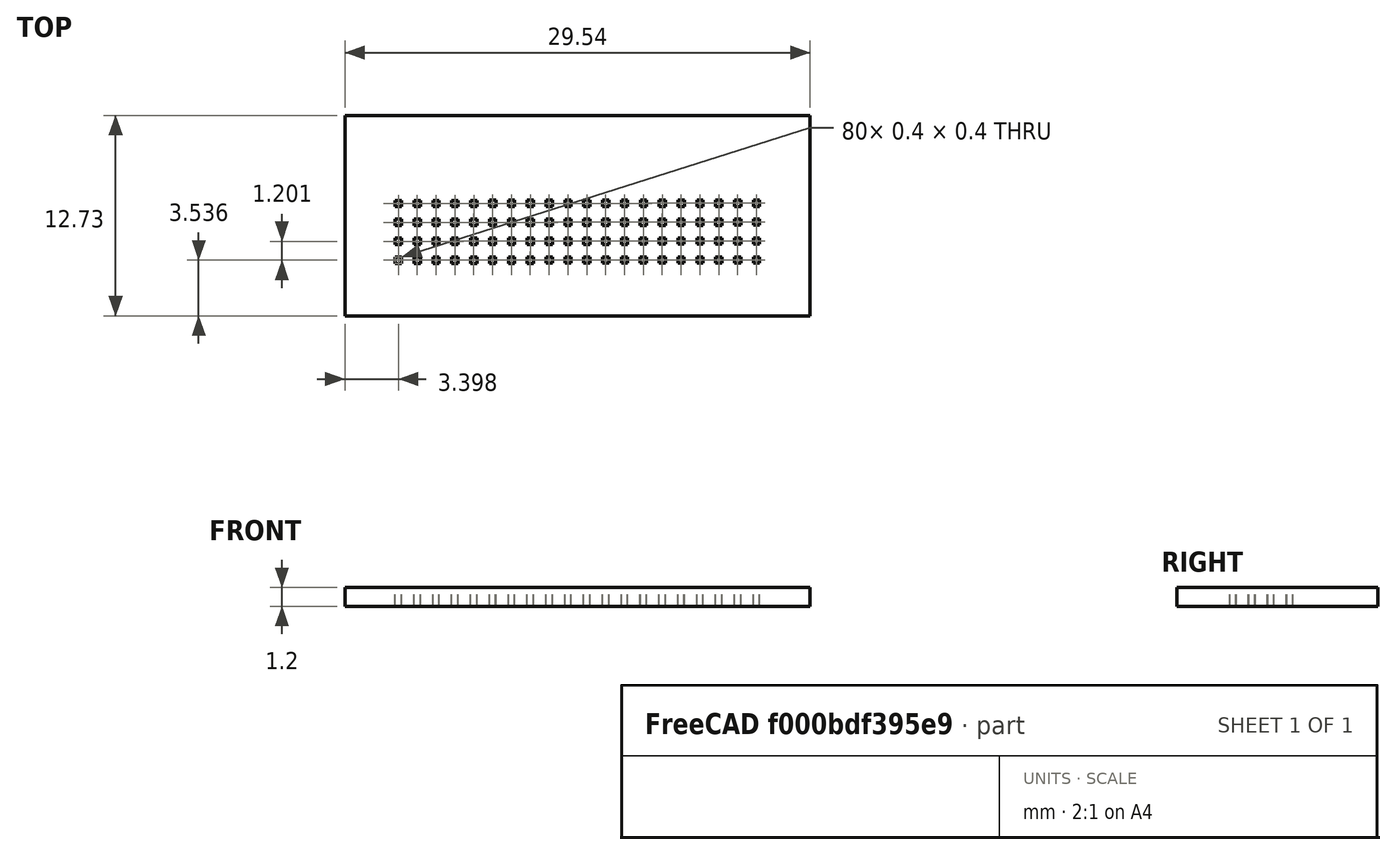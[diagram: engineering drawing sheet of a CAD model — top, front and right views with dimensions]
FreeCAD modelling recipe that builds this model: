
FCSTD DOCUMENT  (FreeCAD 0.17R13519 (Git))
Label: base
License: All rights reserved
LicenseURL: http://en.wikipedia.org/wiki/All_rights_reserved
objects: Sketcher::SketchObject×1, PartDesign::Pad×1, PartDesign::Body×1
note: 4 computed .brp shape members not serialized (recipe doc carries the construction recipe); baked Part::Feature solids carry a one-line shape summary decoded from their .brp

FEATURE [Sketcher::SketchObject] Sketch
  MapMode = 5
  Support = -> [XY_Plane]
  sketch-geometry (335):
    g0: LineSegment [constr] StartX=0 StartY=0 StartZ=0 EndX=31.2 EndY=0 EndZ=0
    g1: LineSegment [constr] StartX=31.2 StartY=0 StartZ=0 EndX=31.2 EndY=31.2 EndZ=0
    g2: LineSegment [constr] StartX=31.2 StartY=31.2 StartZ=0 EndX=0 EndY=31.2 EndZ=0
    g3: LineSegment [constr] StartX=0 StartY=31.2 StartZ=0 EndX=0 EndY=0 EndZ=0
    g4: LineSegment [constr] StartX=4 StartY=4 StartZ=0 EndX=27.2 EndY=4 EndZ=0
    g5: LineSegment [constr] StartX=27.2 StartY=4 StartZ=0 EndX=27.2 EndY=27.2 EndZ=0
    g6: LineSegment [constr] StartX=27.2 StartY=27.2 StartZ=0 EndX=4 EndY=27.2 EndZ=0
    g7: LineSegment [constr] StartX=4 StartY=27.2 StartZ=0 EndX=4 EndY=4 EndZ=0
    g8: LineSegment [constr] StartX=26.74 StartY=26.0196 StartZ=0 EndX=26.74 EndY=25.6196 EndZ=0
    g9: LineSegment [constr] StartX=5.2 StartY=27.2 StartZ=0 EndX=5.2 EndY=28.4271 EndZ=0
    g10: LineSegment StartX=4 StartY=27.2 StartZ=0 EndX=4.4 EndY=27.2 EndZ=0
    g11: LineSegment StartX=4.4 StartY=27.2 StartZ=0 EndX=4.4 EndY=26.8 EndZ=0
    g12: LineSegment StartX=4.4 StartY=26.8 StartZ=0 EndX=4 EndY=26.8 EndZ=0
    g13: LineSegment StartX=4 StartY=26.8 StartZ=0 EndX=4 EndY=27.2 EndZ=0
    g14: LineSegment [constr] StartX=5.2 StartY=26.8 StartZ=0 EndX=5.2 EndY=25.7987 EndZ=0
    g15: LineSegment StartX=5.19695 StartY=27.201 StartZ=0 EndX=5.59695 EndY=27.201 EndZ=0
    g16: LineSegment StartX=5.59695 StartY=27.201 StartZ=0 EndX=5.59695 EndY=26.801 EndZ=0
    g17: LineSegment StartX=5.59695 StartY=26.801 StartZ=0 EndX=5.19695 EndY=26.801 EndZ=0
    g18: LineSegment StartX=5.19695 StartY=26.801 StartZ=0 EndX=5.19695 EndY=27.201 EndZ=0
    g19: LineSegment StartX=6.39391 StartY=27.2021 StartZ=0 EndX=6.79391 EndY=27.2021 EndZ=0
    g20: LineSegment StartX=6.79391 StartY=27.2021 StartZ=0 EndX=6.79391 EndY=26.8021 EndZ=0
    g21: LineSegment StartX=6.79391 StartY=26.8021 StartZ=0 EndX=6.39391 EndY=26.8021 EndZ=0
    g22: LineSegment StartX=6.39391 StartY=26.8021 StartZ=0 EndX=6.39391 EndY=27.2021 EndZ=0
    g23: LineSegment StartX=7.59086 StartY=27.2031 StartZ=0 EndX=7.99086 EndY=27.2031 EndZ=0
    g24: LineSegment StartX=7.99086 StartY=27.2031 StartZ=0 EndX=7.99086 EndY=26.8031 EndZ=0
    g25: LineSegment StartX=7.99086 StartY=26.8031 StartZ=0 EndX=7.59086 EndY=26.8031 EndZ=0
    g26: LineSegment StartX=7.59086 StartY=26.8031 StartZ=0 EndX=7.59086 EndY=27.2031 EndZ=0
    g27: LineSegment StartX=8.78782 StartY=27.2041 StartZ=0 EndX=9.18782 EndY=27.2041 EndZ=0
    g28: LineSegment StartX=9.18782 StartY=27.2041 StartZ=0 EndX=9.18782 EndY=26.8041 EndZ=0
    g29: LineSegment StartX=9.18782 StartY=26.8041 StartZ=0 EndX=8.78782 EndY=26.8041 EndZ=0
    g30: LineSegment StartX=8.78782 StartY=26.8041 StartZ=0 EndX=8.78782 EndY=27.2041 EndZ=0
    g31: LineSegment StartX=9.98477 StartY=27.2052 StartZ=0 EndX=10.3848 EndY=27.2052 EndZ=0
    g32: LineSegment StartX=10.3848 StartY=27.2052 StartZ=0 EndX=10.3848 EndY=26.8052 EndZ=0
    g33: LineSegment StartX=10.3848 StartY=26.8052 StartZ=0 EndX=9.98477 EndY=26.8052 EndZ=0
    g34: LineSegment StartX=9.98477 StartY=26.8052 StartZ=0 EndX=9.98477 EndY=27.2052 EndZ=0
    g35: LineSegment StartX=11.1817 StartY=27.2062 StartZ=0 EndX=11.5817 EndY=27.2062 EndZ=0
    g36: LineSegment StartX=11.5817 StartY=27.2062 StartZ=0 EndX=11.5817 EndY=26.8062 EndZ=0
    g37: LineSegment StartX=11.5817 StartY=26.8062 StartZ=0 EndX=11.1817 EndY=26.8062 EndZ=0
    g38: LineSegment StartX=11.1817 StartY=26.8062 StartZ=0 EndX=11.1817 EndY=27.2062 EndZ=0
    g39: LineSegment StartX=12.3787 StartY=27.2072 StartZ=0 EndX=12.7787 EndY=27.2072 EndZ=0
    g40: LineSegment StartX=12.7787 StartY=27.2072 StartZ=0 EndX=12.7787 EndY=26.8072 EndZ=0
    g41: LineSegment StartX=12.7787 StartY=26.8072 StartZ=0 EndX=12.3787 EndY=26.8072 EndZ=0
    g42: LineSegment StartX=12.3787 StartY=26.8072 StartZ=0 EndX=12.3787 EndY=27.2072 EndZ=0
    g43: LineSegment StartX=13.5756 StartY=27.2083 StartZ=0 EndX=13.9756 EndY=27.2083 EndZ=0
    g44: LineSegment StartX=13.9756 StartY=27.2083 StartZ=0 EndX=13.9756 EndY=26.8083 EndZ=0
    g45: LineSegment StartX=13.9756 StartY=26.8083 StartZ=0 EndX=13.5756 EndY=26.8083 EndZ=0
    g46: LineSegment StartX=13.5756 StartY=26.8083 StartZ=0 EndX=13.5756 EndY=27.2083 EndZ=0
    g47: LineSegment StartX=14.7726 StartY=27.2093 StartZ=0 EndX=15.1726 EndY=27.2093 EndZ=0
    g48: LineSegment StartX=15.1726 StartY=27.2093 StartZ=0 EndX=15.1726 EndY=26.8093 EndZ=0
    g49: LineSegment StartX=15.1726 StartY=26.8093 StartZ=0 EndX=14.7726 EndY=26.8093 EndZ=0
    g50: LineSegment StartX=14.7726 StartY=26.8093 StartZ=0 EndX=14.7726 EndY=27.2093 EndZ=0
    g51: LineSegment StartX=15.9695 StartY=27.2103 StartZ=0 EndX=16.3695 EndY=27.2103 EndZ=0
    g52: LineSegment StartX=16.3695 StartY=27.2103 StartZ=0 EndX=16.3695 EndY=26.8103 EndZ=0
    g53: LineSegment StartX=16.3695 StartY=26.8103 StartZ=0 EndX=15.9695 EndY=26.8103 EndZ=0
    g54: LineSegment StartX=15.9695 StartY=26.8103 StartZ=0 EndX=15.9695 EndY=27.2103 EndZ=0
    g55: LineSegment StartX=17.1665 StartY=27.2114 StartZ=0 EndX=17.5665 EndY=27.2114 EndZ=0
    g56: LineSegment StartX=17.5665 StartY=27.2114 StartZ=0 EndX=17.5665 EndY=26.8114 EndZ=0
    g57: LineSegment StartX=17.5665 StartY=26.8114 StartZ=0 EndX=17.1665 EndY=26.8114 EndZ=0
    g58: LineSegment StartX=17.1665 StartY=26.8114 StartZ=0 EndX=17.1665 EndY=27.2114 EndZ=0
    g59: LineSegment StartX=18.3634 StartY=27.2124 StartZ=0 EndX=18.7634 EndY=27.2124 EndZ=0
    g60: LineSegment StartX=18.7634 StartY=27.2124 StartZ=0 EndX=18.7634 EndY=26.8124 EndZ=0
    g61: LineSegment StartX=18.7634 StartY=26.8124 StartZ=0 EndX=18.3634 EndY=26.8124 EndZ=0
    g62: LineSegment StartX=18.3634 StartY=26.8124 StartZ=0 EndX=18.3634 EndY=27.2124 EndZ=0
    g63: LineSegment StartX=19.5604 StartY=27.2134 StartZ=0 EndX=19.9604 EndY=27.2134 EndZ=0
    g64: LineSegment StartX=19.9604 StartY=27.2134 StartZ=0 EndX=19.9604 EndY=26.8134 EndZ=0
    g65: LineSegment StartX=19.9604 StartY=26.8134 StartZ=0 EndX=19.5604 EndY=26.8134 EndZ=0
    g66: LineSegment StartX=19.5604 StartY=26.8134 StartZ=0 EndX=19.5604 EndY=27.2134 EndZ=0
    g67: LineSegment StartX=20.7574 StartY=27.2144 StartZ=0 EndX=21.1574 EndY=27.2144 EndZ=0
    g68: LineSegment StartX=21.1574 StartY=27.2144 StartZ=0 EndX=21.1574 EndY=26.8144 EndZ=0
    g69: LineSegment StartX=21.1574 StartY=26.8144 StartZ=0 EndX=20.7574 EndY=26.8144 EndZ=0
    g70: LineSegment StartX=20.7574 StartY=26.8144 StartZ=0 EndX=20.7574 EndY=27.2144 EndZ=0
    g71: LineSegment StartX=21.9543 StartY=27.2155 StartZ=0 EndX=22.3543 EndY=27.2155 EndZ=0
    g72: LineSegment StartX=22.3543 StartY=27.2155 StartZ=0 EndX=22.3543 EndY=26.8155 EndZ=0
    g73: LineSegment StartX=22.3543 StartY=26.8155 StartZ=0 EndX=21.9543 EndY=26.8155 EndZ=0
    g74: LineSegment StartX=21.9543 StartY=26.8155 StartZ=0 EndX=21.9543 EndY=27.2155 EndZ=0
    g75: LineSegment StartX=23.1513 StartY=27.2165 StartZ=0 EndX=23.5513 EndY=27.2165 EndZ=0
    g76: LineSegment StartX=23.5513 StartY=27.2165 StartZ=0 EndX=23.5513 EndY=26.8165 EndZ=0
    g77: LineSegment StartX=23.5513 StartY=26.8165 StartZ=0 EndX=23.1513 EndY=26.8165 EndZ=0
    g78: LineSegment StartX=23.1513 StartY=26.8165 StartZ=0 EndX=23.1513 EndY=27.2165 EndZ=0
    g79: LineSegment StartX=24.3482 StartY=27.2175 StartZ=0 EndX=24.7482 EndY=27.2175 EndZ=0
    g80: LineSegment StartX=24.7482 StartY=27.2175 StartZ=0 EndX=24.7482 EndY=26.8175 EndZ=0
    g81: LineSegment StartX=24.7482 StartY=26.8175 StartZ=0 EndX=24.3482 EndY=26.8175 EndZ=0
    g82: LineSegment StartX=24.3482 StartY=26.8175 StartZ=0 EndX=24.3482 EndY=27.2175 EndZ=0
    g83: LineSegment StartX=25.5452 StartY=27.2186 StartZ=0 EndX=25.9452 EndY=27.2186 EndZ=0
    g84: LineSegment StartX=25.9452 StartY=27.2186 StartZ=0 EndX=25.9452 EndY=26.8186 EndZ=0
    g85: LineSegment StartX=25.9452 StartY=26.8186 StartZ=0 EndX=25.5452 EndY=26.8186 EndZ=0
    g86: LineSegment StartX=25.5452 StartY=26.8186 StartZ=0 EndX=25.5452 EndY=27.2186 EndZ=0
    g87: LineSegment StartX=26.74 StartY=27.2196 StartZ=0 EndX=27.1421 EndY=27.2196 EndZ=0
    g88: LineSegment StartX=27.1421 StartY=27.2196 StartZ=0 EndX=27.1421 EndY=26.8196 EndZ=0
    g89: LineSegment StartX=27.1421 StartY=26.8196 StartZ=0 EndX=26.74 EndY=26.8196 EndZ=0
    g90: LineSegment StartX=26.74 StartY=26.8196 StartZ=0 EndX=26.74 EndY=27.2196 EndZ=0
    g91: LineSegment StartX=3.99932 StartY=25.9988 StartZ=0 EndX=4.39932 EndY=25.9988 EndZ=0
    g92: LineSegment StartX=4.39932 StartY=25.9988 StartZ=0 EndX=4.39932 EndY=25.5988 EndZ=0
    g93: LineSegment StartX=4.39932 StartY=25.5988 StartZ=0 EndX=3.99932 EndY=25.5988 EndZ=0
    g94: LineSegment StartX=3.99932 StartY=25.5988 StartZ=0 EndX=3.99932 EndY=25.9988 EndZ=0
    g95: LineSegment StartX=5.19627 StartY=25.9998 StartZ=0 EndX=5.59627 EndY=25.9998 EndZ=0
    g96: LineSegment StartX=5.59627 StartY=25.9998 StartZ=0 EndX=5.59627 EndY=25.5998 EndZ=0
    g97: LineSegment StartX=5.59627 StartY=25.5998 StartZ=0 EndX=5.19627 EndY=25.5998 EndZ=0
    g98: LineSegment StartX=5.19627 StartY=25.5998 StartZ=0 EndX=5.19627 EndY=25.9998 EndZ=0
    g99: LineSegment StartX=6.39322 StartY=26.0009 StartZ=0 EndX=6.79322 EndY=26.0009 EndZ=0
    g100: LineSegment StartX=6.79322 StartY=26.0009 StartZ=0 EndX=6.79322 EndY=25.6009 EndZ=0
    g101: LineSegment StartX=6.79322 StartY=25.6009 StartZ=0 EndX=6.39322 EndY=25.6009 EndZ=0
    g102: LineSegment StartX=6.39322 StartY=25.6009 StartZ=0 EndX=6.39322 EndY=26.0009 EndZ=0
    g103: LineSegment StartX=7.59018 StartY=26.0019 StartZ=0 EndX=7.99018 EndY=26.0019 EndZ=0
    g104: LineSegment StartX=7.99018 StartY=26.0019 StartZ=0 EndX=7.99018 EndY=25.6019 EndZ=0
    g105: LineSegment StartX=7.99018 StartY=25.6019 StartZ=0 EndX=7.59018 EndY=25.6019 EndZ=0
    g106: LineSegment StartX=7.59018 StartY=25.6019 StartZ=0 EndX=7.59018 EndY=26.0019 EndZ=0
    g107: LineSegment StartX=8.78713 StartY=26.0029 StartZ=0 EndX=9.18713 EndY=26.0029 EndZ=0
    g108: LineSegment StartX=9.18713 StartY=26.0029 StartZ=0 EndX=9.18713 EndY=25.6029 EndZ=0
    g109: LineSegment StartX=9.18713 StartY=25.6029 StartZ=0 EndX=8.78713 EndY=25.6029 EndZ=0
    g110: LineSegment StartX=8.78713 StartY=25.6029 StartZ=0 EndX=8.78713 EndY=26.0029 EndZ=0
    g111: LineSegment StartX=9.98409 StartY=26.004 StartZ=0 EndX=10.3841 EndY=26.004 EndZ=0
    g112: LineSegment StartX=10.3841 StartY=26.004 StartZ=0 EndX=10.3841 EndY=25.604 EndZ=0
    g113: LineSegment StartX=10.3841 StartY=25.604 StartZ=0 EndX=9.98409 EndY=25.604 EndZ=0
    g114: LineSegment StartX=9.98409 StartY=25.604 StartZ=0 EndX=9.98409 EndY=26.004 EndZ=0
    g115: LineSegment StartX=11.181 StartY=26.005 StartZ=0 EndX=11.581 EndY=26.005 EndZ=0
    g116: LineSegment StartX=11.581 StartY=26.005 StartZ=0 EndX=11.581 EndY=25.605 EndZ=0
    g117: LineSegment StartX=11.581 StartY=25.605 StartZ=0 EndX=11.181 EndY=25.605 EndZ=0
    g118: LineSegment StartX=11.181 StartY=25.605 StartZ=0 EndX=11.181 EndY=26.005 EndZ=0
    g119: LineSegment StartX=12.378 StartY=26.006 StartZ=0 EndX=12.778 EndY=26.006 EndZ=0
    g120: LineSegment StartX=12.778 StartY=26.006 StartZ=0 EndX=12.778 EndY=25.606 EndZ=0
    g121: LineSegment StartX=12.778 StartY=25.606 StartZ=0 EndX=12.378 EndY=25.606 EndZ=0
    g122: LineSegment StartX=12.378 StartY=25.606 StartZ=0 EndX=12.378 EndY=26.006 EndZ=0
    g123: LineSegment StartX=13.5749 StartY=26.0071 StartZ=0 EndX=13.9749 EndY=26.0071 EndZ=0
    g124: LineSegment StartX=13.9749 StartY=26.0071 StartZ=0 EndX=13.9749 EndY=25.6071 EndZ=0
    g125: LineSegment StartX=13.9749 StartY=25.6071 StartZ=0 EndX=13.5749 EndY=25.6071 EndZ=0
    g126: LineSegment StartX=13.5749 StartY=25.6071 StartZ=0 EndX=13.5749 EndY=26.0071 EndZ=0
    g127: LineSegment StartX=14.7719 StartY=26.0081 StartZ=0 EndX=15.1719 EndY=26.0081 EndZ=0
    g128: LineSegment StartX=15.1719 StartY=26.0081 StartZ=0 EndX=15.1719 EndY=25.6081 EndZ=0
    g129: LineSegment StartX=15.1719 StartY=25.6081 StartZ=0 EndX=14.7719 EndY=25.6081 EndZ=0
    g130: LineSegment StartX=14.7719 StartY=25.6081 StartZ=0 EndX=14.7719 EndY=26.0081 EndZ=0
    g131: LineSegment StartX=15.9689 StartY=26.0091 StartZ=0 EndX=16.3689 EndY=26.0091 EndZ=0
    g132: LineSegment StartX=16.3689 StartY=26.0091 StartZ=0 EndX=16.3689 EndY=25.6091 EndZ=0
    g133: LineSegment StartX=16.3689 StartY=25.6091 StartZ=0 EndX=15.9689 EndY=25.6091 EndZ=0
    g134: LineSegment StartX=15.9689 StartY=25.6091 StartZ=0 EndX=15.9689 EndY=26.0091 EndZ=0
    g135: LineSegment StartX=17.1658 StartY=26.0102 StartZ=0 EndX=17.5658 EndY=26.0102 EndZ=0
    g136: LineSegment StartX=17.5658 StartY=26.0102 StartZ=0 EndX=17.5658 EndY=25.6102 EndZ=0
    g137: LineSegment StartX=17.5658 StartY=25.6102 StartZ=0 EndX=17.1658 EndY=25.6102 EndZ=0
    g138: LineSegment StartX=17.1658 StartY=25.6102 StartZ=0 EndX=17.1658 EndY=26.0102 EndZ=0
    g139: LineSegment StartX=18.3628 StartY=26.0112 StartZ=0 EndX=18.7628 EndY=26.0112 EndZ=0
    g140: LineSegment StartX=18.7628 StartY=26.0112 StartZ=0 EndX=18.7628 EndY=25.6112 EndZ=0
    g141: LineSegment StartX=18.7628 StartY=25.6112 StartZ=0 EndX=18.3628 EndY=25.6112 EndZ=0
    g142: LineSegment StartX=18.3628 StartY=25.6112 StartZ=0 EndX=18.3628 EndY=26.0112 EndZ=0
    g143: LineSegment StartX=19.5597 StartY=26.0122 StartZ=0 EndX=19.9597 EndY=26.0122 EndZ=0
    g144: LineSegment StartX=19.9597 StartY=26.0122 StartZ=0 EndX=19.9597 EndY=25.6122 EndZ=0
    g145: LineSegment StartX=19.9597 StartY=25.6122 StartZ=0 EndX=19.5597 EndY=25.6122 EndZ=0
    g146: LineSegment StartX=19.5597 StartY=25.6122 StartZ=0 EndX=19.5597 EndY=26.0122 EndZ=0
    g147: LineSegment StartX=20.7567 StartY=26.0132 StartZ=0 EndX=21.1567 EndY=26.0132 EndZ=0
    g148: LineSegment StartX=21.1567 StartY=26.0132 StartZ=0 EndX=21.1567 EndY=25.6132 EndZ=0
    g149: LineSegment StartX=21.1567 StartY=25.6132 StartZ=0 EndX=20.7567 EndY=25.6132 EndZ=0
    g150: LineSegment StartX=20.7567 StartY=25.6132 StartZ=0 EndX=20.7567 EndY=26.0132 EndZ=0
    g151: LineSegment StartX=21.9536 StartY=26.0143 StartZ=0 EndX=22.3536 EndY=26.0143 EndZ=0
    g152: LineSegment StartX=22.3536 StartY=26.0143 StartZ=0 EndX=22.3536 EndY=25.6143 EndZ=0
    g153: LineSegment StartX=22.3536 StartY=25.6143 StartZ=0 EndX=21.9536 EndY=25.6143 EndZ=0
    g154: LineSegment StartX=21.9536 StartY=25.6143 StartZ=0 EndX=21.9536 EndY=26.0143 EndZ=0
    g155: LineSegment StartX=23.1506 StartY=26.0153 StartZ=0 EndX=23.5506 EndY=26.0153 EndZ=0
    g156: LineSegment StartX=23.5506 StartY=26.0153 StartZ=0 EndX=23.5506 EndY=25.6153 EndZ=0
    g157: LineSegment StartX=23.5506 StartY=25.6153 StartZ=0 EndX=23.1506 EndY=25.6153 EndZ=0
    g158: LineSegment StartX=23.1506 StartY=25.6153 StartZ=0 EndX=23.1506 EndY=26.0153 EndZ=0
    g159: LineSegment StartX=24.3475 StartY=26.0163 StartZ=0 EndX=24.7475 EndY=26.0163 EndZ=0
    g160: LineSegment StartX=24.7475 StartY=26.0163 StartZ=0 EndX=24.7475 EndY=25.6163 EndZ=0
    g161: LineSegment StartX=24.7475 StartY=25.6163 StartZ=0 EndX=24.3475 EndY=25.6163 EndZ=0
    g162: LineSegment StartX=24.3475 StartY=25.6163 StartZ=0 EndX=24.3475 EndY=26.0163 EndZ=0
    g163: LineSegment StartX=25.5445 StartY=26.0174 StartZ=0 EndX=25.9445 EndY=26.0174 EndZ=0
    g164: LineSegment StartX=25.9445 StartY=26.0174 StartZ=0 EndX=25.9445 EndY=25.6174 EndZ=0
    g165: LineSegment StartX=25.9445 StartY=25.6174 StartZ=0 EndX=25.5445 EndY=25.6174 EndZ=0
    g166: LineSegment StartX=25.5445 StartY=25.6174 StartZ=0 EndX=25.5445 EndY=26.0174 EndZ=0
    g167: LineSegment StartX=26.74 StartY=26.0184 StartZ=0 EndX=27.1414 EndY=26.0184 EndZ=0
    g168: LineSegment StartX=27.1414 StartY=26.0184 StartZ=0 EndX=27.1414 EndY=25.6196 EndZ=0
    g169: LineSegment StartX=27.1414 StartY=25.6196 StartZ=0 EndX=26.74 EndY=25.6196 EndZ=0
    g170: LineSegment StartX=26.74 StartY=25.6196 StartZ=0 EndX=26.74 EndY=26.0184 EndZ=0
    g171: LineSegment StartX=3.99863 StartY=24.7976 StartZ=0 EndX=4.39863 EndY=24.7976 EndZ=0
    g172: LineSegment StartX=4.39863 StartY=24.7976 StartZ=0 EndX=4.39863 EndY=24.3976 EndZ=0
    g173: LineSegment StartX=4.39863 StartY=24.3976 StartZ=0 EndX=3.99863 EndY=24.3976 EndZ=0
    g174: LineSegment StartX=3.99863 StartY=24.3976 StartZ=0 EndX=3.99863 EndY=24.7976 EndZ=0
    g175: LineSegment StartX=5.19559 StartY=24.7986 StartZ=0 EndX=5.59559 EndY=24.7986 EndZ=0
    g176: LineSegment StartX=5.59559 StartY=24.7986 StartZ=0 EndX=5.59559 EndY=24.3986 EndZ=0
    g177: LineSegment StartX=5.59559 StartY=24.3986 StartZ=0 EndX=5.19559 EndY=24.3986 EndZ=0
    g178: LineSegment StartX=5.19559 StartY=24.3986 StartZ=0 EndX=5.19559 EndY=24.7986 EndZ=0
    g179: LineSegment StartX=6.39254 StartY=24.7997 StartZ=0 EndX=6.79254 EndY=24.7997 EndZ=0
    g180: LineSegment StartX=6.79254 StartY=24.7997 StartZ=0 EndX=6.79254 EndY=24.3997 EndZ=0
    g181: LineSegment StartX=6.79254 StartY=24.3997 StartZ=0 EndX=6.39254 EndY=24.3997 EndZ=0
    g182: LineSegment StartX=6.39254 StartY=24.3997 StartZ=0 EndX=6.39254 EndY=24.7997 EndZ=0
    g183: LineSegment StartX=7.58949 StartY=24.8007 StartZ=0 EndX=7.98949 EndY=24.8007 EndZ=0
    g184: LineSegment StartX=7.98949 StartY=24.8007 StartZ=0 EndX=7.98949 EndY=24.4007 EndZ=0
    g185: LineSegment StartX=7.98949 StartY=24.4007 StartZ=0 EndX=7.58949 EndY=24.4007 EndZ=0
    g186: LineSegment StartX=7.58949 StartY=24.4007 StartZ=0 EndX=7.58949 EndY=24.8007 EndZ=0
    g187: LineSegment StartX=8.78645 StartY=24.8017 StartZ=0 EndX=9.18645 EndY=24.8017 EndZ=0
    g188: LineSegment StartX=9.18645 StartY=24.8017 StartZ=0 EndX=9.18645 EndY=24.4017 EndZ=0
    g189: LineSegment StartX=9.18645 StartY=24.4017 StartZ=0 EndX=8.78645 EndY=24.4017 EndZ=0
    g190: LineSegment StartX=8.78645 StartY=24.4017 StartZ=0 EndX=8.78645 EndY=24.8017 EndZ=0
    g191: LineSegment StartX=9.9834 StartY=24.8028 StartZ=0 EndX=10.3834 EndY=24.8028 EndZ=0
    g192: LineSegment StartX=10.3834 StartY=24.8028 StartZ=0 EndX=10.3834 EndY=24.4028 EndZ=0
    g193: LineSegment StartX=10.3834 StartY=24.4028 StartZ=0 EndX=9.9834 EndY=24.4028 EndZ=0
    g194: LineSegment StartX=9.9834 StartY=24.4028 StartZ=0 EndX=9.9834 EndY=24.8028 EndZ=0
    g195: LineSegment StartX=11.1804 StartY=24.8038 StartZ=0 EndX=11.5804 EndY=24.8038 EndZ=0
    g196: LineSegment StartX=11.5804 StartY=24.8038 StartZ=0 EndX=11.5804 EndY=24.4038 EndZ=0
    g197: LineSegment StartX=11.5804 StartY=24.4038 StartZ=0 EndX=11.1804 EndY=24.4038 EndZ=0
    g198: LineSegment StartX=11.1804 StartY=24.4038 StartZ=0 EndX=11.1804 EndY=24.8038 EndZ=0
    g199: LineSegment StartX=12.3773 StartY=24.8048 StartZ=0 EndX=12.7773 EndY=24.8048 EndZ=0
    g200: LineSegment StartX=12.7773 StartY=24.8048 StartZ=0 EndX=12.7773 EndY=24.4048 EndZ=0
    g201: LineSegment StartX=12.7773 StartY=24.4048 StartZ=0 EndX=12.3773 EndY=24.4048 EndZ=0
    g202: LineSegment StartX=12.3773 StartY=24.4048 StartZ=0 EndX=12.3773 EndY=24.8048 EndZ=0
    g203: LineSegment StartX=13.5743 StartY=24.8059 StartZ=0 EndX=13.9743 EndY=24.8059 EndZ=0
    g204: LineSegment StartX=13.9743 StartY=24.8059 StartZ=0 EndX=13.9743 EndY=24.4059 EndZ=0
    g205: LineSegment StartX=13.9743 StartY=24.4059 StartZ=0 EndX=13.5743 EndY=24.4059 EndZ=0
    g206: LineSegment StartX=13.5743 StartY=24.4059 StartZ=0 EndX=13.5743 EndY=24.8059 EndZ=0
    g207: LineSegment StartX=14.7712 StartY=24.8069 StartZ=0 EndX=15.1712 EndY=24.8069 EndZ=0
    g208: LineSegment StartX=15.1712 StartY=24.8069 StartZ=0 EndX=15.1712 EndY=24.4069 EndZ=0
    g209: LineSegment StartX=15.1712 StartY=24.4069 StartZ=0 EndX=14.7712 EndY=24.4069 EndZ=0
    g210: LineSegment StartX=14.7712 StartY=24.4069 StartZ=0 EndX=14.7712 EndY=24.8069 EndZ=0
    g211: LineSegment StartX=15.9682 StartY=24.8079 StartZ=0 EndX=16.3682 EndY=24.8079 EndZ=0
    g212: LineSegment StartX=16.3682 StartY=24.8079 StartZ=0 EndX=16.3682 EndY=24.4079 EndZ=0
    g213: LineSegment StartX=16.3682 StartY=24.4079 StartZ=0 EndX=15.9682 EndY=24.4079 EndZ=0
    g214: LineSegment StartX=15.9682 StartY=24.4079 StartZ=0 EndX=15.9682 EndY=24.8079 EndZ=0
    g215: LineSegment StartX=17.1651 StartY=24.8089 StartZ=0 EndX=17.5651 EndY=24.8089 EndZ=0
    g216: LineSegment StartX=17.5651 StartY=24.8089 StartZ=0 EndX=17.5651 EndY=24.409 EndZ=0
    g217: LineSegment StartX=17.5651 StartY=24.409 StartZ=0 EndX=17.1651 EndY=24.409 EndZ=0
    g218: LineSegment StartX=17.1651 StartY=24.409 StartZ=0 EndX=17.1651 EndY=24.8089 EndZ=0
    g219: LineSegment StartX=18.3621 StartY=24.81 StartZ=0 EndX=18.7621 EndY=24.81 EndZ=0
    g220: LineSegment StartX=18.7621 StartY=24.81 StartZ=0 EndX=18.7621 EndY=24.41 EndZ=0
    g221: LineSegment StartX=18.7621 StartY=24.41 StartZ=0 EndX=18.3621 EndY=24.41 EndZ=0
    g222: LineSegment StartX=18.3621 StartY=24.41 StartZ=0 EndX=18.3621 EndY=24.81 EndZ=0
    g223: LineSegment StartX=19.559 StartY=24.811 StartZ=0 EndX=19.959 EndY=24.811 EndZ=0
    g224: LineSegment StartX=19.959 StartY=24.811 StartZ=0 EndX=19.959 EndY=24.411 EndZ=0
    g225: LineSegment StartX=19.959 StartY=24.411 StartZ=0 EndX=19.559 EndY=24.411 EndZ=0
    g226: LineSegment StartX=19.559 StartY=24.411 StartZ=0 EndX=19.559 EndY=24.811 EndZ=0
    g227: LineSegment StartX=20.756 StartY=24.812 StartZ=0 EndX=21.156 EndY=24.812 EndZ=0
    g228: LineSegment StartX=21.156 StartY=24.812 StartZ=0 EndX=21.156 EndY=24.412 EndZ=0
    g229: LineSegment StartX=21.156 StartY=24.412 StartZ=0 EndX=20.756 EndY=24.412 EndZ=0
    g230: LineSegment StartX=20.756 StartY=24.412 StartZ=0 EndX=20.756 EndY=24.812 EndZ=0
    g231: LineSegment StartX=21.9529 StartY=24.8131 StartZ=0 EndX=22.3529 EndY=24.8131 EndZ=0
    g232: LineSegment StartX=22.3529 StartY=24.8131 StartZ=0 EndX=22.3529 EndY=24.4131 EndZ=0
    g233: LineSegment StartX=22.3529 StartY=24.4131 StartZ=0 EndX=21.9529 EndY=24.4131 EndZ=0
    g234: LineSegment StartX=21.9529 StartY=24.4131 StartZ=0 EndX=21.9529 EndY=24.8131 EndZ=0
    g235: LineSegment StartX=23.1499 StartY=24.8141 StartZ=0 EndX=23.5499 EndY=24.8141 EndZ=0
    g236: LineSegment StartX=23.5499 StartY=24.8141 StartZ=0 EndX=23.5499 EndY=24.4141 EndZ=0
    g237: LineSegment StartX=23.5499 StartY=24.4141 StartZ=0 EndX=23.1499 EndY=24.4141 EndZ=0
    g238: LineSegment StartX=23.1499 StartY=24.4141 StartZ=0 EndX=23.1499 EndY=24.8141 EndZ=0
    g239: LineSegment StartX=24.3468 StartY=24.8151 StartZ=0 EndX=24.7468 EndY=24.8151 EndZ=0
    g240: LineSegment StartX=24.7468 StartY=24.8151 StartZ=0 EndX=24.7468 EndY=24.4151 EndZ=0
    g241: LineSegment StartX=24.7468 StartY=24.4151 StartZ=0 EndX=24.3468 EndY=24.4151 EndZ=0
    g242: LineSegment StartX=24.3468 StartY=24.4151 StartZ=0 EndX=24.3468 EndY=24.8151 EndZ=0
    g243: LineSegment StartX=25.5438 StartY=24.8162 StartZ=0 EndX=25.9438 EndY=24.8162 EndZ=0
    g244: LineSegment StartX=25.9438 StartY=24.8162 StartZ=0 EndX=25.9438 EndY=24.4162 EndZ=0
    g245: LineSegment StartX=25.9438 StartY=24.4162 StartZ=0 EndX=25.5438 EndY=24.4162 EndZ=0
    g246: LineSegment StartX=25.5438 StartY=24.4162 StartZ=0 EndX=25.5438 EndY=24.8162 EndZ=0
    g247: LineSegment StartX=26.7386 StartY=24.8172 StartZ=0 EndX=27.1408 EndY=24.8172 EndZ=0
    g248: LineSegment StartX=27.1408 StartY=24.8172 StartZ=0 EndX=27.1408 EndY=24.4172 EndZ=0
    g249: LineSegment StartX=27.1408 StartY=24.4172 StartZ=0 EndX=26.7386 EndY=24.4172 EndZ=0
    g250: LineSegment StartX=26.7386 StartY=24.4172 StartZ=0 EndX=26.7386 EndY=24.8172 EndZ=0
    g251: LineSegment StartX=3.99795 StartY=23.5964 StartZ=0 EndX=4.39795 EndY=23.5964 EndZ=0
    g252: LineSegment StartX=4.39795 StartY=23.5964 StartZ=0 EndX=4.39795 EndY=23.1964 EndZ=0
    g253: LineSegment StartX=4.39795 StartY=23.1964 StartZ=0 EndX=3.99795 EndY=23.1964 EndZ=0
    g254: LineSegment StartX=3.99795 StartY=23.1964 StartZ=0 EndX=3.99795 EndY=23.5964 EndZ=0
    g255: LineSegment StartX=5.1949 StartY=23.5974 StartZ=0 EndX=5.5949 EndY=23.5974 EndZ=0
    g256: LineSegment StartX=5.5949 StartY=23.5974 StartZ=0 EndX=5.5949 EndY=23.1974 EndZ=0
    g257: LineSegment StartX=5.5949 StartY=23.1974 StartZ=0 EndX=5.1949 EndY=23.1974 EndZ=0
    g258: LineSegment StartX=5.1949 StartY=23.1974 StartZ=0 EndX=5.1949 EndY=23.5974 EndZ=0
    g259: LineSegment StartX=6.39186 StartY=23.5985 StartZ=0 EndX=6.79186 EndY=23.5985 EndZ=0
    g260: LineSegment StartX=6.79186 StartY=23.5985 StartZ=0 EndX=6.79186 EndY=23.1985 EndZ=0
    g261: LineSegment StartX=6.79186 StartY=23.1985 StartZ=0 EndX=6.39186 EndY=23.1985 EndZ=0
    g262: LineSegment StartX=6.39186 StartY=23.1985 StartZ=0 EndX=6.39186 EndY=23.5985 EndZ=0
    g263: LineSegment StartX=7.58881 StartY=23.5995 StartZ=0 EndX=7.98881 EndY=23.5995 EndZ=0
    g264: LineSegment StartX=7.98881 StartY=23.5995 StartZ=0 EndX=7.98881 EndY=23.1995 EndZ=0
    g265: LineSegment StartX=7.98881 StartY=23.1995 StartZ=0 EndX=7.58881 EndY=23.1995 EndZ=0
    g266: LineSegment StartX=7.58881 StartY=23.1995 StartZ=0 EndX=7.58881 EndY=23.5995 EndZ=0
    g267: LineSegment StartX=8.78576 StartY=23.6005 StartZ=0 EndX=9.18576 EndY=23.6005 EndZ=0
    g268: LineSegment StartX=9.18576 StartY=23.6005 StartZ=0 EndX=9.18576 EndY=23.2005 EndZ=0
    g269: LineSegment StartX=9.18576 StartY=23.2005 StartZ=0 EndX=8.78576 EndY=23.2005 EndZ=0
    g270: LineSegment StartX=8.78576 StartY=23.2005 StartZ=0 EndX=8.78576 EndY=23.6005 EndZ=0
    g271: LineSegment StartX=9.98272 StartY=23.6016 StartZ=0 EndX=10.3827 EndY=23.6016 EndZ=0
    g272: LineSegment StartX=10.3827 StartY=23.6016 StartZ=0 EndX=10.3827 EndY=23.2016 EndZ=0
    g273: LineSegment StartX=10.3827 StartY=23.2016 StartZ=0 EndX=9.98272 EndY=23.2016 EndZ=0
    g274: LineSegment StartX=9.98272 StartY=23.2016 StartZ=0 EndX=9.98272 EndY=23.6016 EndZ=0
    g275: LineSegment StartX=11.1797 StartY=23.6026 StartZ=0 EndX=11.5797 EndY=23.6026 EndZ=0
    g276: LineSegment StartX=11.5797 StartY=23.6026 StartZ=0 EndX=11.5797 EndY=23.2026 EndZ=0
    g277: LineSegment StartX=11.5797 StartY=23.2026 StartZ=0 EndX=11.1797 EndY=23.2026 EndZ=0
    g278: LineSegment StartX=11.1797 StartY=23.2026 StartZ=0 EndX=11.1797 EndY=23.6026 EndZ=0
    g279: LineSegment StartX=12.3766 StartY=23.6036 StartZ=0 EndX=12.7766 EndY=23.6036 EndZ=0
    g280: LineSegment StartX=12.7766 StartY=23.6036 StartZ=0 EndX=12.7766 EndY=23.2036 EndZ=0
    g281: LineSegment StartX=12.7766 StartY=23.2036 StartZ=0 EndX=12.3766 EndY=23.2036 EndZ=0
    g282: LineSegment StartX=12.3766 StartY=23.2036 StartZ=0 EndX=12.3766 EndY=23.6036 EndZ=0
    g283: LineSegment StartX=13.5736 StartY=23.6047 StartZ=0 EndX=13.9736 EndY=23.6047 EndZ=0
    g284: LineSegment StartX=13.9736 StartY=23.6047 StartZ=0 EndX=13.9736 EndY=23.2047 EndZ=0
    g285: LineSegment StartX=13.9736 StartY=23.2047 StartZ=0 EndX=13.5736 EndY=23.2047 EndZ=0
    g286: LineSegment StartX=13.5736 StartY=23.2047 StartZ=0 EndX=13.5736 EndY=23.6047 EndZ=0
    g287: LineSegment StartX=14.7705 StartY=23.6057 StartZ=0 EndX=15.1705 EndY=23.6057 EndZ=0
    g288: LineSegment StartX=15.1705 StartY=23.6057 StartZ=0 EndX=15.1705 EndY=23.2057 EndZ=0
    g289: LineSegment StartX=15.1705 StartY=23.2057 StartZ=0 EndX=14.7705 EndY=23.2057 EndZ=0
    g290: LineSegment StartX=14.7705 StartY=23.2057 StartZ=0 EndX=14.7705 EndY=23.6057 EndZ=0
    g291: LineSegment StartX=15.9675 StartY=23.6067 StartZ=0 EndX=16.3675 EndY=23.6067 EndZ=0
    g292: LineSegment StartX=16.3675 StartY=23.6067 StartZ=0 EndX=16.3675 EndY=23.2067 EndZ=0
    g293: LineSegment StartX=16.3675 StartY=23.2067 StartZ=0 EndX=15.9675 EndY=23.2067 EndZ=0
    g294: LineSegment StartX=15.9675 StartY=23.2067 StartZ=0 EndX=15.9675 EndY=23.6067 EndZ=0
    g295: LineSegment StartX=17.1644 StartY=23.6077 StartZ=0 EndX=17.5644 EndY=23.6077 EndZ=0
    g296: LineSegment StartX=17.5644 StartY=23.6077 StartZ=0 EndX=17.5644 EndY=23.2077 EndZ=0
    g297: LineSegment StartX=17.5644 StartY=23.2077 StartZ=0 EndX=17.1644 EndY=23.2077 EndZ=0
    g298: LineSegment StartX=17.1644 StartY=23.2077 StartZ=0 EndX=17.1644 EndY=23.6077 EndZ=0
    g299: LineSegment StartX=18.3614 StartY=23.6088 StartZ=0 EndX=18.7614 EndY=23.6088 EndZ=0
    g300: LineSegment StartX=18.7614 StartY=23.6088 StartZ=0 EndX=18.7614 EndY=23.2088 EndZ=0
    g301: LineSegment StartX=18.7614 StartY=23.2088 StartZ=0 EndX=18.3614 EndY=23.2088 EndZ=0
    g302: LineSegment StartX=18.3614 StartY=23.2088 StartZ=0 EndX=18.3614 EndY=23.6088 EndZ=0
    g303: LineSegment StartX=19.5584 StartY=23.6098 StartZ=0 EndX=19.9583 EndY=23.6098 EndZ=0
    g304: LineSegment StartX=19.9583 StartY=23.6098 StartZ=0 EndX=19.9583 EndY=23.2098 EndZ=0
    g305: LineSegment StartX=19.9583 StartY=23.2098 StartZ=0 EndX=19.5584 EndY=23.2098 EndZ=0
    g306: LineSegment StartX=19.5584 StartY=23.2098 StartZ=0 EndX=19.5584 EndY=23.6098 EndZ=0
    g307: LineSegment StartX=20.7553 StartY=23.6108 StartZ=0 EndX=21.1553 EndY=23.6108 EndZ=0
    g308: LineSegment StartX=21.1553 StartY=23.6108 StartZ=0 EndX=21.1553 EndY=23.2108 EndZ=0
    g309: LineSegment StartX=21.1553 StartY=23.2108 StartZ=0 EndX=20.7553 EndY=23.2108 EndZ=0
    g310: LineSegment StartX=20.7553 StartY=23.2108 StartZ=0 EndX=20.7553 EndY=23.6108 EndZ=0
    g311: LineSegment StartX=21.9523 StartY=23.6119 StartZ=0 EndX=22.3523 EndY=23.6119 EndZ=0
    g312: LineSegment StartX=22.3523 StartY=23.6119 StartZ=0 EndX=22.3523 EndY=23.2119 EndZ=0
    g313: LineSegment StartX=22.3523 StartY=23.2119 StartZ=0 EndX=21.9523 EndY=23.2119 EndZ=0
    g314: LineSegment StartX=21.9523 StartY=23.2119 StartZ=0 EndX=21.9523 EndY=23.6119 EndZ=0
    g315: LineSegment StartX=23.1492 StartY=23.6129 StartZ=0 EndX=23.5492 EndY=23.6129 EndZ=0
    g316: LineSegment StartX=23.5492 StartY=23.6129 StartZ=0 EndX=23.5492 EndY=23.2129 EndZ=0
    g317: LineSegment StartX=23.5492 StartY=23.2129 StartZ=0 EndX=23.1492 EndY=23.2129 EndZ=0
    g318: LineSegment StartX=23.1492 StartY=23.2129 StartZ=0 EndX=23.1492 EndY=23.6129 EndZ=0
    g319: LineSegment StartX=24.3462 StartY=23.6139 StartZ=0 EndX=24.7462 EndY=23.6139 EndZ=0
    g320: LineSegment StartX=24.7462 StartY=23.6139 StartZ=0 EndX=24.7462 EndY=23.2139 EndZ=0
    g321: LineSegment StartX=24.7462 StartY=23.2139 StartZ=0 EndX=24.3462 EndY=23.2139 EndZ=0
    g322: LineSegment StartX=24.3462 StartY=23.2139 StartZ=0 EndX=24.3462 EndY=23.6139 EndZ=0
    g323: LineSegment StartX=25.5431 StartY=23.615 StartZ=0 EndX=25.9431 EndY=23.615 EndZ=0
    g324: LineSegment StartX=25.9431 StartY=23.615 StartZ=0 EndX=25.9431 EndY=23.215 EndZ=0
    g325: LineSegment StartX=25.9431 StartY=23.215 StartZ=0 EndX=25.5431 EndY=23.215 EndZ=0
    g326: LineSegment StartX=25.5431 StartY=23.215 StartZ=0 EndX=25.5431 EndY=23.615 EndZ=0
    g327: LineSegment StartX=26.7379 StartY=23.616 StartZ=0 EndX=27.1401 EndY=23.616 EndZ=0
    g328: LineSegment StartX=27.1401 StartY=23.616 StartZ=0 EndX=27.1401 EndY=23.216 EndZ=0
    g329: LineSegment StartX=27.1401 StartY=23.216 StartZ=0 EndX=26.7379 EndY=23.216 EndZ=0
    g330: LineSegment StartX=26.7379 StartY=23.216 StartZ=0 EndX=26.7379 EndY=23.616 EndZ=0
    g331: LineSegment StartX=0.803983 StartY=32.5923 StartZ=0 EndX=30.3422 EndY=32.5923 EndZ=0
    g332: LineSegment StartX=30.3422 StartY=32.5923 StartZ=0 EndX=30.3422 EndY=19.8566 EndZ=0
    g333: LineSegment StartX=30.3422 StartY=19.8566 StartZ=0 EndX=0.803983 EndY=19.8566 EndZ=0
    g334: LineSegment StartX=0.803983 StartY=19.8566 StartZ=0 EndX=0.803983 EndY=32.5923 EndZ=0
  constraints (684):
    c: Coincident(g0,g1)
    c: Coincident(g1,g2)
    c: Coincident(g2,g3)
    c: Coincident(g3,g0)
    c: Horizontal(g0)
    c: Horizontal(g2)
    c: Vertical(g1)
    c: Vertical(g3)
    c: Coincident(g0,g-1)
    c: Coincident(g4,g5)
    c: Coincident(g7,g4)
    c: Horizontal(g4)
    c: Vertical(g5)
    c: DistanceX(g-1,g4) = 4
    c: DistanceY(g-1,g4) = 4
    c: DistanceX(g4,g0) = 4
    c: DistanceY(g5,g1) = 4
    c: Vertical(g8)
    c: Distance(g4) = 23.2
    c: Distance(g7) = 23.2
    c: Coincident(g6,g5)
    c: Coincident(g6,g7)
    c: Horizontal(g6)
    c: PointOnObject(g9,g6)
    c: Vertical(g9)
    c: Distance(g9,g6) = 1.2
    c: Vertical(g7)
    c: Coincident(g10,g11)
    c: Coincident(g11,g12)
    c: Coincident(g12,g13)
    c: Coincident(g13,g10)
    c: Horizontal(g10)
    c: Horizontal(g12)
    c: Vertical(g11)
    c: Vertical(g13)
    c: Coincident(g10,g6)
    c: Vertical(g14)
    c: Vertical(g14,g9)
    c: Distance(g14,g9) = 0.4
    c: Coincident(g15,g16)
    c: Coincident(g16,g17)
    c: Coincident(g17,g18)
    c: Coincident(g18,g15)
    c: Horizontal(g15)
    c: Horizontal(g17)
    c: Vertical(g16)
    c: Vertical(g18)
    c: Coincident(g19,g20)
    c: Coincident(g20,g21)
    c: Coincident(g21,g22)
    c: Coincident(g22,g19)
    c: Horizontal(g19)
    c: Horizontal(g21)
    c: Vertical(g20)
    c: Vertical(g22)
    c: Coincident(g23,g24)
    c: Coincident(g24,g25)
    c: Coincident(g25,g26)
    c: Coincident(g26,g23)
    c: Horizontal(g23)
    c: Horizontal(g25)
    c: Vertical(g24)
    c: Vertical(g26)
    c: Coincident(g27,g28)
    c: Coincident(g28,g29)
    c: Coincident(g29,g30)
    c: Coincident(g30,g27)
    c: Horizontal(g27)
    c: Horizontal(g29)
    c: Vertical(g28)
    c: Vertical(g30)
    c: Coincident(g31,g32)
    c: Coincident(g32,g33)
    c: Coincident(g33,g34)
    c: Coincident(g34,g31)
    c: Horizontal(g31)
    c: Horizontal(g33)
    c: Vertical(g32)
    c: Vertical(g34)
    c: Coincident(g35,g36)
    c: Coincident(g36,g37)
    c: Coincident(g37,g38)
    c: Coincident(g38,g35)
    c: Horizontal(g35)
    c: Horizontal(g37)
    c: Vertical(g36)
    c: Vertical(g38)
    c: Coincident(g39,g40)
    c: Coincident(g40,g41)
    c: Coincident(g41,g42)
    c: Coincident(g42,g39)
    c: Horizontal(g39)
    c: Horizontal(g41)
    c: Vertical(g40)
    c: Vertical(g42)
    c: Coincident(g43,g44)
    c: Coincident(g44,g45)
    c: Coincident(g45,g46)
    c: Coincident(g46,g43)
    c: Horizontal(g43)
    c: Horizontal(g45)
    c: Vertical(g44)
    c: Vertical(g46)
    c: Coincident(g47,g48)
    c: Coincident(g48,g49)
    c: Coincident(g49,g50)
    c: Coincident(g50,g47)
    c: Horizontal(g47)
    c: Horizontal(g49)
    c: Vertical(g48)
    c: Vertical(g50)
    c: Coincident(g51,g52)
    c: Coincident(g52,g53)
    c: Coincident(g53,g54)
    c: Coincident(g54,g51)
    c: Horizontal(g51)
    c: Horizontal(g53)
    c: Vertical(g52)
    c: Vertical(g54)
    c: Coincident(g55,g56)
    c: Coincident(g56,g57)
    c: Coincident(g57,g58)
    c: Coincident(g58,g55)
    c: Horizontal(g55)
    c: Horizontal(g57)
    c: Vertical(g56)
    c: Vertical(g58)
    c: Coincident(g59,g60)
    c: Coincident(g60,g61)
    c: Coincident(g61,g62)
    c: Coincident(g62,g59)
    c: Horizontal(g59)
    c: Horizontal(g61)
    c: Vertical(g60)
    c: Vertical(g62)
    c: Coincident(g63,g64)
    c: Coincident(g64,g65)
    c: Coincident(g65,g66)
    c: Coincident(g66,g63)
    c: Horizontal(g63)
    c: Horizontal(g65)
    c: Vertical(g64)
    c: Vertical(g66)
    c: Coincident(g67,g68)
    c: Coincident(g68,g69)
    c: Coincident(g69,g70)
    c: Coincident(g70,g67)
    c: Horizontal(g67)
    c: Horizontal(g69)
    c: Vertical(g68)
    c: Vertical(g70)
    c: Coincident(g71,g72)
    c: Coincident(g72,g73)
    c: Coincident(g73,g74)
    c: Coincident(g74,g71)
    c: Horizontal(g71)
    c: Horizontal(g73)
    c: Vertical(g72)
    c: Vertical(g74)
    c: Coincident(g75,g76)
    c: Coincident(g76,g77)
    c: Coincident(g77,g78)
    c: Coincident(g78,g75)
    c: Horizontal(g75)
    c: Horizontal(g77)
    c: Vertical(g76)
    c: Vertical(g78)
    c: Coincident(g79,g80)
    c: Coincident(g80,g81)
    c: Coincident(g81,g82)
    c: Coincident(g82,g79)
    c: Horizontal(g79)
    c: Horizontal(g81)
    c: Vertical(g80)
    c: Vertical(g82)
    c: Coincident(g83,g84)
    c: Coincident(g84,g85)
    c: Coincident(g85,g86)
    c: Coincident(g86,g83)
    c: Horizontal(g83)
    c: Horizontal(g85)
    c: Vertical(g84)
    c: Vertical(g86)
    c: Coincident(g87,g88)
    c: Coincident(g88,g89)
    c: Coincident(g89,g90)
    c: Coincident(g90,g87)
    c: Horizontal(g87)
    c: Horizontal(g89)
    c: Vertical(g88)
    c: Vertical(g90)
    c: Distance(g87,g6) = 22.74
    c: Distance(g8) = 0.4
    c: Vertical(g8,g87)
    c: Distance(g87,g8) = 1.2
    c: Coincident(g91,g92)
    c: Coincident(g92,g93)
    c: Coincident(g93,g94)
    c: Coincident(g94,g91)
    c: Horizontal(g91)
    c: Horizontal(g93)
    c: Vertical(g92)
    c: Vertical(g94)
    c: Coincident(g95,g96)
    c: Coincident(g96,g97)
    c: Coincident(g97,g98)
    c: Coincident(g98,g95)
    c: Horizontal(g95)
    c: Horizontal(g97)
    c: Vertical(g96)
    c: Vertical(g98)
    c: Coincident(g99,g100)
    c: Coincident(g100,g101)
    c: Coincident(g101,g102)
    c: Coincident(g102,g99)
    c: Horizontal(g99)
    c: Horizontal(g101)
    c: Vertical(g100)
    c: Vertical(g102)
    c: Coincident(g103,g104)
    c: Coincident(g104,g105)
    c: Coincident(g105,g106)
    c: Coincident(g106,g103)
    c: Horizontal(g103)
    c: Horizontal(g105)
    c: Vertical(g104)
    c: Vertical(g106)
    c: Coincident(g107,g108)
    c: Coincident(g108,g109)
    c: Coincident(g109,g110)
    c: Coincident(g110,g107)
    c: Horizontal(g107)
    c: Horizontal(g109)
    c: Vertical(g108)
    c: Vertical(g110)
    c: Coincident(g111,g112)
    c: Coincident(g112,g113)
    c: Coincident(g113,g114)
    c: Coincident(g114,g111)
    c: Horizontal(g111)
    c: Horizontal(g113)
    c: Vertical(g112)
    c: Vertical(g114)
    c: Coincident(g115,g116)
    c: Coincident(g116,g117)
    c: Coincident(g117,g118)
    c: Coincident(g118,g115)
    c: Horizontal(g115)
    c: Horizontal(g117)
    c: Vertical(g116)
    c: Vertical(g118)
    c: Coincident(g119,g120)
    c: Coincident(g120,g121)
    c: Coincident(g121,g122)
    c: Coincident(g122,g119)
    c: Horizontal(g119)
    c: Horizontal(g121)
    c: Vertical(g120)
    c: Vertical(g122)
    c: Coincident(g123,g124)
    c: Coincident(g124,g125)
    c: Coincident(g125,g126)
    c: Coincident(g126,g123)
    c: Horizontal(g123)
    c: Horizontal(g125)
    c: Vertical(g124)
    c: Vertical(g126)
    c: Coincident(g127,g128)
    c: Coincident(g128,g129)
    c: Coincident(g129,g130)
    c: Coincident(g130,g127)
    c: Horizontal(g127)
    c: Horizontal(g129)
    c: Vertical(g128)
    c: Vertical(g130)
    c: Coincident(g131,g132)
    c: Coincident(g132,g133)
    c: Coincident(g133,g134)
    c: Coincident(g134,g131)
    c: Horizontal(g131)
    c: Horizontal(g133)
    c: Vertical(g132)
    c: Vertical(g134)
    c: Coincident(g135,g136)
    c: Coincident(g136,g137)
    c: Coincident(g137,g138)
    c: Coincident(g138,g135)
    c: Horizontal(g135)
    c: Horizontal(g137)
    c: Vertical(g136)
    c: Vertical(g138)
    c: Coincident(g139,g140)
    c: Coincident(g140,g141)
    c: Coincident(g141,g142)
    c: Coincident(g142,g139)
    c: Horizontal(g139)
    c: Horizontal(g141)
    c: Vertical(g140)
    c: Vertical(g142)
    c: Coincident(g143,g144)
    c: Coincident(g144,g145)
    c: Coincident(g145,g146)
    c: Coincident(g146,g143)
    c: Horizontal(g143)
    c: Horizontal(g145)
    c: Vertical(g144)
    c: Vertical(g146)
    c: Coincident(g147,g148)
    c: Coincident(g148,g149)
    c: Coincident(g149,g150)
    c: Coincident(g150,g147)
    c: Horizontal(g147)
    c: Horizontal(g149)
    c: Vertical(g148)
    c: Vertical(g150)
    c: Coincident(g151,g152)
    c: Coincident(g152,g153)
    c: Coincident(g153,g154)
    c: Coincident(g154,g151)
    c: Horizontal(g151)
    c: Horizontal(g153)
    c: Vertical(g152)
    c: Vertical(g154)
    c: Coincident(g155,g156)
    c: Coincident(g156,g157)
    c: Coincident(g157,g158)
    c: Coincident(g158,g155)
    c: Horizontal(g155)
    c: Horizontal(g157)
    c: Vertical(g156)
    c: Vertical(g158)
    c: Coincident(g159,g160)
    c: Coincident(g160,g161)
    c: Coincident(g161,g162)
    c: Coincident(g162,g159)
    c: Horizontal(g159)
    c: Horizontal(g161)
    c: Vertical(g160)
    c: Vertical(g162)
    c: Coincident(g163,g164)
    c: Coincident(g164,g165)
    c: Coincident(g165,g166)
    c: Coincident(g166,g163)
    c: Horizontal(g163)
    c: Horizontal(g165)
    c: Vertical(g164)
    c: Vertical(g166)
    c: Coincident(g167,g168)
    c: Coincident(g168,g169)
    c: Coincident(g169,g170)
    c: Coincident(g170,g167)
    c: Horizontal(g167)
    c: Horizontal(g169)
    c: Vertical(g168)
    c: Vertical(g170)
    c: Coincident(g171,g172)
    c: Coincident(g172,g173)
    c: Coincident(g173,g174)
    c: Coincident(g174,g171)
    c: Horizontal(g171)
    c: Horizontal(g173)
    c: Vertical(g172)
    c: Vertical(g174)
    c: Coincident(g175,g176)
    c: Coincident(g176,g177)
    c: Coincident(g177,g178)
    c: Coincident(g178,g175)
    c: Horizontal(g175)
    c: Horizontal(g177)
    c: Vertical(g176)
    c: Vertical(g178)
    c: Coincident(g179,g180)
    c: Coincident(g180,g181)
    c: Coincident(g181,g182)
    c: Coincident(g182,g179)
    c: Horizontal(g179)
    c: Horizontal(g181)
    c: Vertical(g180)
    c: Vertical(g182)
    c: Coincident(g183,g184)
    c: Coincident(g184,g185)
    c: Coincident(g185,g186)
    c: Coincident(g186,g183)
    c: Horizontal(g183)
    c: Horizontal(g185)
    c: Vertical(g184)
    c: Vertical(g186)
    c: Coincident(g187,g188)
    c: Coincident(g188,g189)
    c: Coincident(g189,g190)
    c: Coincident(g190,g187)
    c: Horizontal(g187)
    c: Horizontal(g189)
    c: Vertical(g188)
    c: Vertical(g190)
    c: Coincident(g191,g192)
    c: Coincident(g192,g193)
    c: Coincident(g193,g194)
    c: Coincident(g194,g191)
    c: Horizontal(g191)
    c: Horizontal(g193)
    c: Vertical(g192)
    c: Vertical(g194)
    c: Coincident(g195,g196)
    c: Coincident(g196,g197)
    c: Coincident(g197,g198)
    c: Coincident(g198,g195)
    c: Horizontal(g195)
    c: Horizontal(g197)
    c: Vertical(g196)
    c: Vertical(g198)
    c: Coincident(g199,g200)
    c: Coincident(g200,g201)
    c: Coincident(g201,g202)
    c: Coincident(g202,g199)
    c: Horizontal(g199)
    c: Horizontal(g201)
    c: Vertical(g200)
    c: Vertical(g202)
    c: Coincident(g203,g204)
    c: Coincident(g204,g205)
    c: Coincident(g205,g206)
    c: Coincident(g206,g203)
    c: Horizontal(g203)
    c: Horizontal(g205)
    c: Vertical(g204)
    c: Vertical(g206)
    c: Coincident(g207,g208)
    c: Coincident(g208,g209)
    c: Coincident(g209,g210)
    c: Coincident(g210,g207)
    c: Horizontal(g207)
    c: Horizontal(g209)
    c: Vertical(g208)
    c: Vertical(g210)
    c: Coincident(g211,g212)
    c: Coincident(g212,g213)
    c: Coincident(g213,g214)
    c: Coincident(g214,g211)
    c: Horizontal(g211)
    c: Horizontal(g213)
    c: Vertical(g212)
    c: Vertical(g214)
    c: Coincident(g215,g216)
    c: Coincident(g216,g217)
    c: Coincident(g217,g218)
    c: Coincident(g218,g215)
    c: Horizontal(g215)
    c: Horizontal(g217)
    c: Vertical(g216)
    c: Vertical(g218)
    c: Coincident(g219,g220)
    c: Coincident(g220,g221)
    c: Coincident(g221,g222)
    c: Coincident(g222,g219)
    c: Horizontal(g219)
    c: Horizontal(g221)
    c: Vertical(g220)
    c: Vertical(g222)
    c: Coincident(g223,g224)
    c: Coincident(g224,g225)
    c: Coincident(g225,g226)
    c: Coincident(g226,g223)
    c: Horizontal(g223)
    c: Horizontal(g225)
    c: Vertical(g224)
    c: Vertical(g226)
    c: Coincident(g227,g228)
    c: Coincident(g228,g229)
    c: Coincident(g229,g230)
    c: Coincident(g230,g227)
    c: Horizontal(g227)
    c: Horizontal(g229)
    c: Vertical(g228)
    c: Vertical(g230)
    c: Coincident(g231,g232)
    c: Coincident(g232,g233)
    c: Coincident(g233,g234)
    c: Coincident(g234,g231)
    c: Horizontal(g231)
    c: Horizontal(g233)
    c: Vertical(g232)
    c: Vertical(g234)
    c: Coincident(g235,g236)
    c: Coincident(g236,g237)
    c: Coincident(g237,g238)
    c: Coincident(g238,g235)
    c: Horizontal(g235)
    c: Horizontal(g237)
    c: Vertical(g236)
    c: Vertical(g238)
    c: Coincident(g239,g240)
    c: Coincident(g240,g241)
    c: Coincident(g241,g242)
    c: Coincident(g242,g239)
    c: Horizontal(g239)
    c: Horizontal(g241)
    c: Vertical(g240)
    c: Vertical(g242)
    c: Coincident(g243,g244)
    c: Coincident(g244,g245)
    c: Coincident(g245,g246)
    c: Coincident(g246,g243)
    c: Horizontal(g243)
    c: Horizontal(g245)
    c: Vertical(g244)
    c: Vertical(g246)
    c: Coincident(g247,g248)
    c: Coincident(g248,g249)
    c: Coincident(g249,g250)
    c: Coincident(g250,g247)
    c: Horizontal(g247)
    c: Horizontal(g249)
    c: Vertical(g248)
    c: Vertical(g250)
    c: Coincident(g251,g252)
    c: Coincident(g252,g253)
    c: Coincident(g253,g254)
    c: Coincident(g254,g251)
    c: Horizontal(g251)
    c: Horizontal(g253)
    c: Vertical(g252)
    c: Vertical(g254)
    c: Coincident(g255,g256)
    c: Coincident(g256,g257)
    c: Coincident(g257,g258)
    c: Coincident(g258,g255)
    c: Horizontal(g255)
    c: Horizontal(g257)
    c: Vertical(g256)
    c: Vertical(g258)
    c: Coincident(g259,g260)
    c: Coincident(g260,g261)
    c: Coincident(g261,g262)
    c: Coincident(g262,g259)
    c: Horizontal(g259)
    c: Horizontal(g261)
    c: Vertical(g260)
    c: Vertical(g262)
    c: Coincident(g263,g264)
    c: Coincident(g264,g265)
    c: Coincident(g265,g266)
    c: Coincident(g266,g263)
    c: Horizontal(g263)
    c: Horizontal(g265)
    c: Vertical(g264)
    c: Vertical(g266)
    c: Coincident(g267,g268)
    c: Coincident(g268,g269)
    c: Coincident(g269,g270)
    c: Coincident(g270,g267)
    c: Horizontal(g267)
    c: Horizontal(g269)
    c: Vertical(g268)
    c: Vertical(g270)
    c: Coincident(g271,g272)
    c: Coincident(g272,g273)
    c: Coincident(g273,g274)
    c: Coincident(g274,g271)
    c: Horizontal(g271)
    c: Horizontal(g273)
    c: Vertical(g272)
    c: Vertical(g274)
    c: Coincident(g275,g276)
    c: Coincident(g276,g277)
    c: Coincident(g277,g278)
    c: Coincident(g278,g275)
    c: Horizontal(g275)
    c: Horizontal(g277)
    c: Vertical(g276)
    c: Vertical(g278)
    c: Coincident(g279,g280)
    c: Coincident(g280,g281)
    c: Coincident(g281,g282)
    c: Coincident(g282,g279)
    c: Horizontal(g279)
    c: Horizontal(g281)
    c: Vertical(g280)
    c: Vertical(g282)
    c: Coincident(g283,g284)
    c: Coincident(g284,g285)
    c: Coincident(g285,g286)
    c: Coincident(g286,g283)
    c: Horizontal(g283)
    c: Horizontal(g285)
    c: Vertical(g284)
    c: Vertical(g286)
    c: Coincident(g287,g288)
    c: Coincident(g288,g289)
    c: Coincident(g289,g290)
    c: Coincident(g290,g287)
    c: Horizontal(g287)
    c: Horizontal(g289)
    c: Vertical(g288)
    c: Vertical(g290)
    c: Coincident(g291,g292)
    c: Coincident(g292,g293)
    c: Coincident(g293,g294)
    c: Coincident(g294,g291)
    c: Horizontal(g291)
    c: Horizontal(g293)
    c: Vertical(g292)
    c: Vertical(g294)
    c: Coincident(g295,g296)
    c: Coincident(g296,g297)
    c: Coincident(g297,g298)
    c: Coincident(g298,g295)
    c: Horizontal(g295)
    c: Horizontal(g297)
    c: Vertical(g296)
    c: Vertical(g298)
    c: Coincident(g299,g300)
    c: Coincident(g300,g301)
    c: Coincident(g301,g302)
    c: Coincident(g302,g299)
    c: Horizontal(g299)
    c: Horizontal(g301)
    c: Vertical(g300)
    c: Vertical(g302)
    c: Coincident(g303,g304)
    c: Coincident(g304,g305)
    c: Coincident(g305,g306)
    c: Coincident(g306,g303)
    c: Horizontal(g303)
    c: Horizontal(g305)
    c: Vertical(g304)
    c: Vertical(g306)
    c: Coincident(g307,g308)
    c: Coincident(g308,g309)
    c: Coincident(g309,g310)
    c: Coincident(g310,g307)
    c: Horizontal(g307)
    c: Horizontal(g309)
    c: Vertical(g308)
    c: Vertical(g310)
    c: Coincident(g311,g312)
    c: Coincident(g312,g313)
    c: Coincident(g313,g314)
    c: Coincident(g314,g311)
    c: Horizontal(g311)
    c: Horizontal(g313)
    c: Vertical(g312)
    c: Vertical(g314)
    c: Coincident(g315,g316)
    c: Coincident(g316,g317)
    c: Coincident(g317,g318)
    c: Coincident(g318,g315)
    c: Horizontal(g315)
    c: Horizontal(g317)
    c: Vertical(g316)
    c: Vertical(g318)
    c: Coincident(g319,g320)
    c: Coincident(g320,g321)
    c: Coincident(g321,g322)
    c: Coincident(g322,g319)
    c: Horizontal(g319)
    c: Horizontal(g321)
    c: Vertical(g320)
    c: Vertical(g322)
    c: Coincident(g323,g324)
    c: Coincident(g324,g325)
    c: Coincident(g325,g326)
    c: Coincident(g326,g323)
    c: Horizontal(g323)
    c: Horizontal(g325)
    c: Vertical(g324)
    c: Vertical(g326)
    c: Coincident(g327,g328)
    c: Coincident(g328,g329)
    c: Coincident(g329,g330)
    c: Coincident(g330,g327)
    c: Horizontal(g327)
    c: Horizontal(g329)
    c: Vertical(g328)
    c: Vertical(g330)
    c: Coincident(g170,g8)
    c: Coincident(g331,g332)
    c: Coincident(g332,g333)
    c: Coincident(g333,g334)
    c: Coincident(g334,g331)
    c: Horizontal(g331)
    c: Horizontal(g333)
    c: Vertical(g332)
    c: Vertical(g334)
FEATURE [PartDesign::Pad] Pad
  Length = 1.2
  Length2 = 100
  Profile = -> Sketch
  Type = 0
FEATURE [PartDesign::Body] Body
  Group = -> [Sketch,Pad]
  Origin = -> Origin
  Tip = -> Pad
